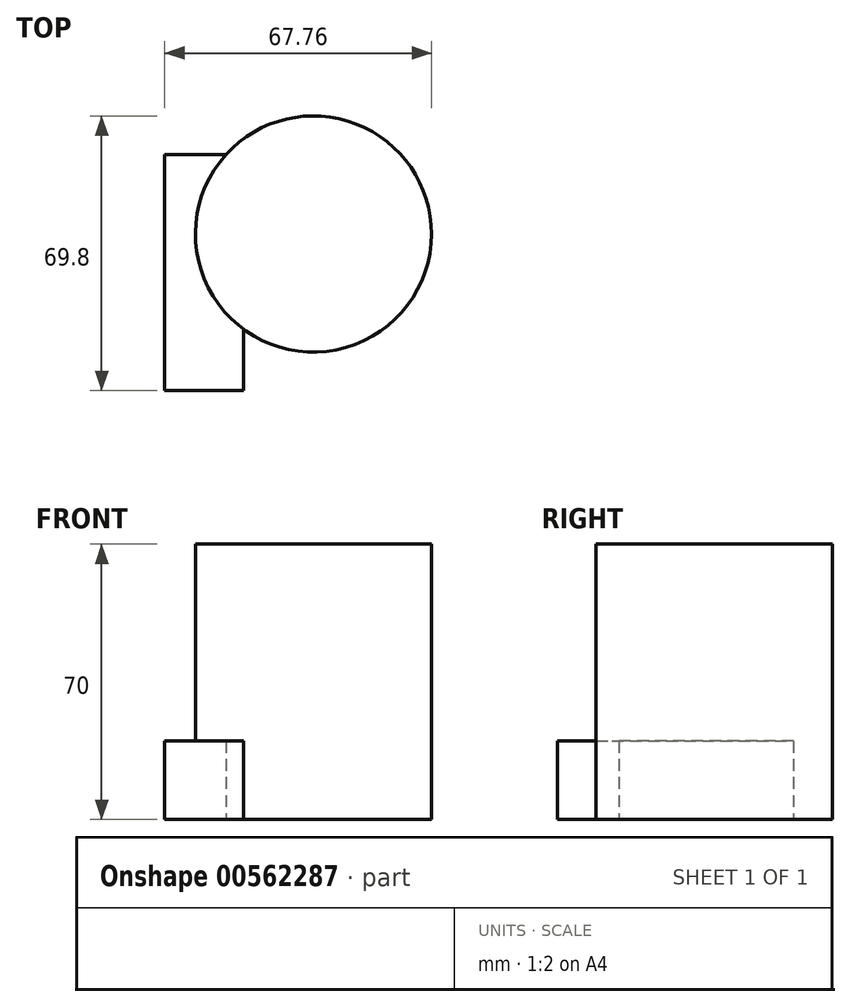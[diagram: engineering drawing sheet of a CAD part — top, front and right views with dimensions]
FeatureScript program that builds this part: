
annotation { "Feature Type Name" : "Feature", "Feature Type Description" : "" }
export const myFeature = defineFeature(function(context is Context, id is Id, definition is map)
    precondition{}
    {
        {
            var Q0;
            Q0=qCreatedBy(makeId("Top.planeOp"),FACE);
            var sketch = newSketch(context, id + "F0", { "sketchPlane" : qUnion([Q0])});
            skCircle(sketch, "E0", {"center": v(17.76, -20.2) * mm, "radius": 30 * mm});
            skSolve(sketch);
        }
        {
            var Q0;
            Q0=makeQuery(id+"F0.imprint","IMPRINT",FACE,{"disambiguationData":[TD([[makeQuery(id+"F0.imprint","IMPRINT",EDGE,{"derivedFrom":sQuery(id+"F0.wireOp",EDGE,"E0")}),1.0]])]});
            extrude(context, id + "F1", {"entities" : qUnion([Q0]), "depth" : 70 * mm, "offsetDistance" : 25 * mm});
        }
        {
            var Q0;
            Q0=qCreatedBy(makeId("Front.planeOp"),FACE);
            var sketch = newSketch(context, id + "F2", { "sketchPlane" : qUnion([Q0])});
            skLineSegment(sketch, "E1.bottom", {"start": v(-20, 0) * mm, "end": v(0, 0) * mm});
            skLineSegment(sketch, "E1.top", {"start": v(-20, 20) * mm, "end": v(0, 20) * mm});
            skLineSegment(sketch, "E1.left", {"start": v(-20, 0) * mm, "end": v(-20, 20) * mm});
            skLineSegment(sketch, "E1.right", {"start": v(0, 0) * mm, "end": v(0, 20) * mm});
            skSolve(sketch);
        }
        {
            var Q0;
            Q0=makeQuery(id+"F2.imprint","IMPRINT",FACE,{"disambiguationData":[TD([[makeQuery(id+"F2.imprint","IMPRINT",EDGE,{"derivedFrom":sQuery(id+"F2.wireOp",EDGE,"E1.bottom")}),1.0]])]});
            extrude(context, id + "F3", {"entities" : qUnion([Q0]), "operationType" : NewBodyOperationType.ADD, "depth" : 60 * mm, "offsetDistance" : 25 * mm});
        }
    });
